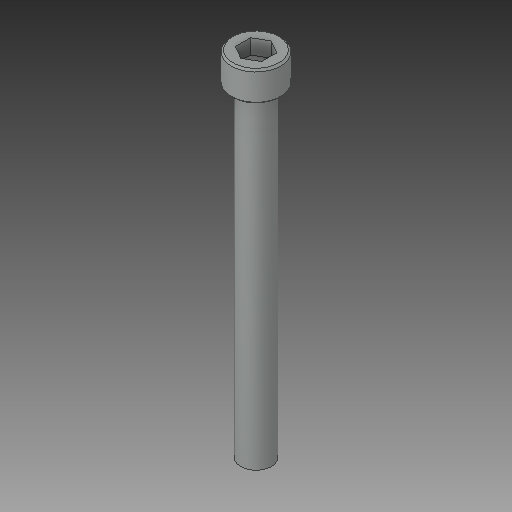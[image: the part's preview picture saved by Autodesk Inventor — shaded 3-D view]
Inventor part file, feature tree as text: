
AUTODESK INVENTOR PART (.ipt)
format: ipt  version: 2018 (Build 220112000, 112)  size: 94,208 bytes
history: native  units: in
note: dims shown in document units (in); Inventor stores cm internally (conversion verified against a paired STEP export)
features: chamfer x1
ambient origin geometry x8: Origin, YZ Plane, XZ Plane, XY Plane, X Axis, Y Axis, Z Axis, Center Point
bodies: Solid1 (feature_tree)
feature tree (1):
  chamfer  "Chamfer2"  [1 undecoded]
note: 1 required parameter value undecoded (feature->parameter linkage not recoverable at this tier; creation-order binding heuristic only, values carry confidence <= 0.55)
